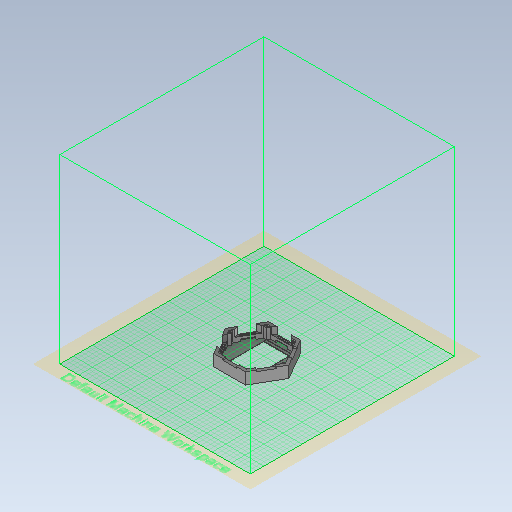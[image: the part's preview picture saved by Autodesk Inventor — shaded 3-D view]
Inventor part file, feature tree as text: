
AUTODESK INVENTOR PART (.ipt)
format: ipt  version: 2020 (Build 240168000, 168)  size: 680,960 bytes
history: native  units: mm
features: extrude x7, other x5, sketch x3, pattern_circular x1
ambient origin geometry x8: Origin, YZ Plane, XZ Plane, XY Plane, X Axis, Y Axis, Z Axis, Center Point
bodies: Body1 (feature_tree)
feature tree (16):
  sketch  "Sketch6"  dims[d72=6.5mm d85=1.0mm d86=0.0mm]
  extrude  "Fronte"  Depth=1.0mm TaperAngle=0.0deg
  extrude  "Esterno"  Depth=6.5mm
  extrude  "Strip"  Depth=2.0mm
  extrude  "Passacavi"  Depth=2.0mm
  extrude  "ScavoStrip"  Depth=26.0mm
  extrude  "SupportoViti"  Depth=2.5mm
  pattern_circular  "RipetizioneFori"  [2 undecoded]
  extrude  "Trasparenza"  TaperAngle=135.0deg  [1 undecoded]
  sketch  "Sketch7"  dims[d87=15.0mm d88=6.5mm]
  other  "Work Axis3"
  other  "Work Axis4"
  other  "Work Axis5"
  other  "Work Axis6"
  other  "Work Axis7"
  sketch  "Sketch11"  dims[d91=2.0mm d92=2.0mm d95=1.25mm d96=26.0mm d97=2.5mm d98=26.0mm d99=135.0deg d100=0.0mm d101=25.0mm d102=0.0mm d103=10.0mm d104=0.0mm d105=11.0mm d106=0.0mm d107=5.0mm d108=0.0mm d114=1.7mm d115=23.0mm d116=0.0mm d117=3.0mm d121=3.0mm d123=6.0mm d124=60.0mm d125=360.0deg d127=140.0mm d128=5.196152mm d129=5.196152mm d130=3.0mm d158=110.0mm d159=50.0mm d160=30.0mm d162=60.0mm d164=360.0deg d166=0.5mm d167=0.0mm d168=2.0mm]
note: 3 required parameter values undecoded (feature->parameter linkage not recoverable at this tier; creation-order binding heuristic only, values carry confidence <= 0.55)
